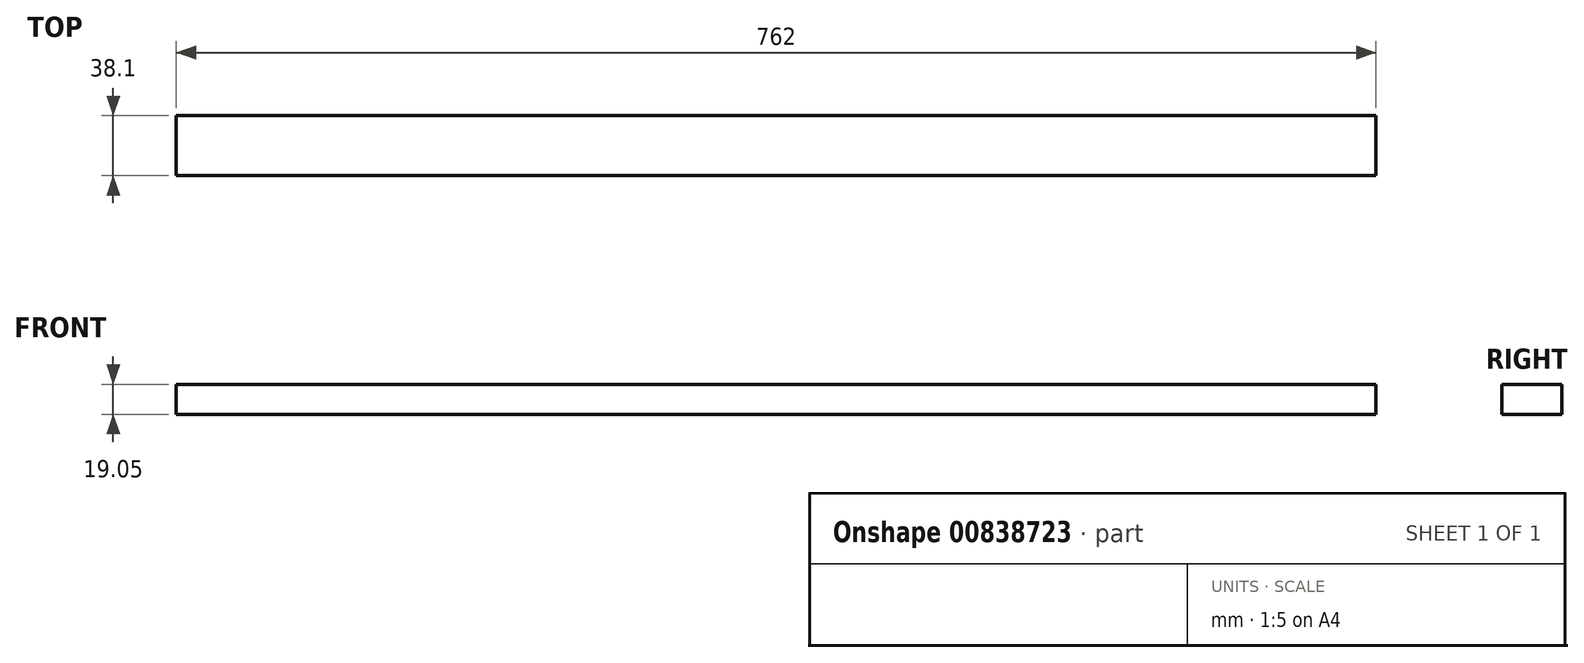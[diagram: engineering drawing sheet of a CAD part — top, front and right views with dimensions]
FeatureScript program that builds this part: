
annotation { "Feature Type Name" : "Feature", "Feature Type Description" : "" }
export const myFeature = defineFeature(function(context is Context, id is Id, definition is map)
    precondition{}
    {
        {
            var Q0;
            Q0=qCreatedBy(makeId("Front.planeOp"),FACE);
            var sketch = newSketch(context, id + "F0", { "sketchPlane" : qUnion([Q0])});
            skLineSegment(sketch, "E0.bottom", {"start": v(0, 0) * mm, "end": v(-762, 0) * mm});
            skLineSegment(sketch, "E0.top", {"start": v(0, 19.05) * mm, "end": v(-762, 19.05) * mm});
            skLineSegment(sketch, "E0.left", {"start": v(0, 0) * mm, "end": v(0, 19.05) * mm});
            skLineSegment(sketch, "E0.right", {"start": v(-762, 0) * mm, "end": v(-762, 19.05) * mm});
            skSolve(sketch);
        }
        {
            var Q0;
            Q0 = qSketchRegion(id + "F0", true);
            extrude(context, id + "F1", {"entities" : qUnion([Q0]), "depth" : 38.1 * mm, "offsetDistance" : 25.4 * mm});
        }
    });
